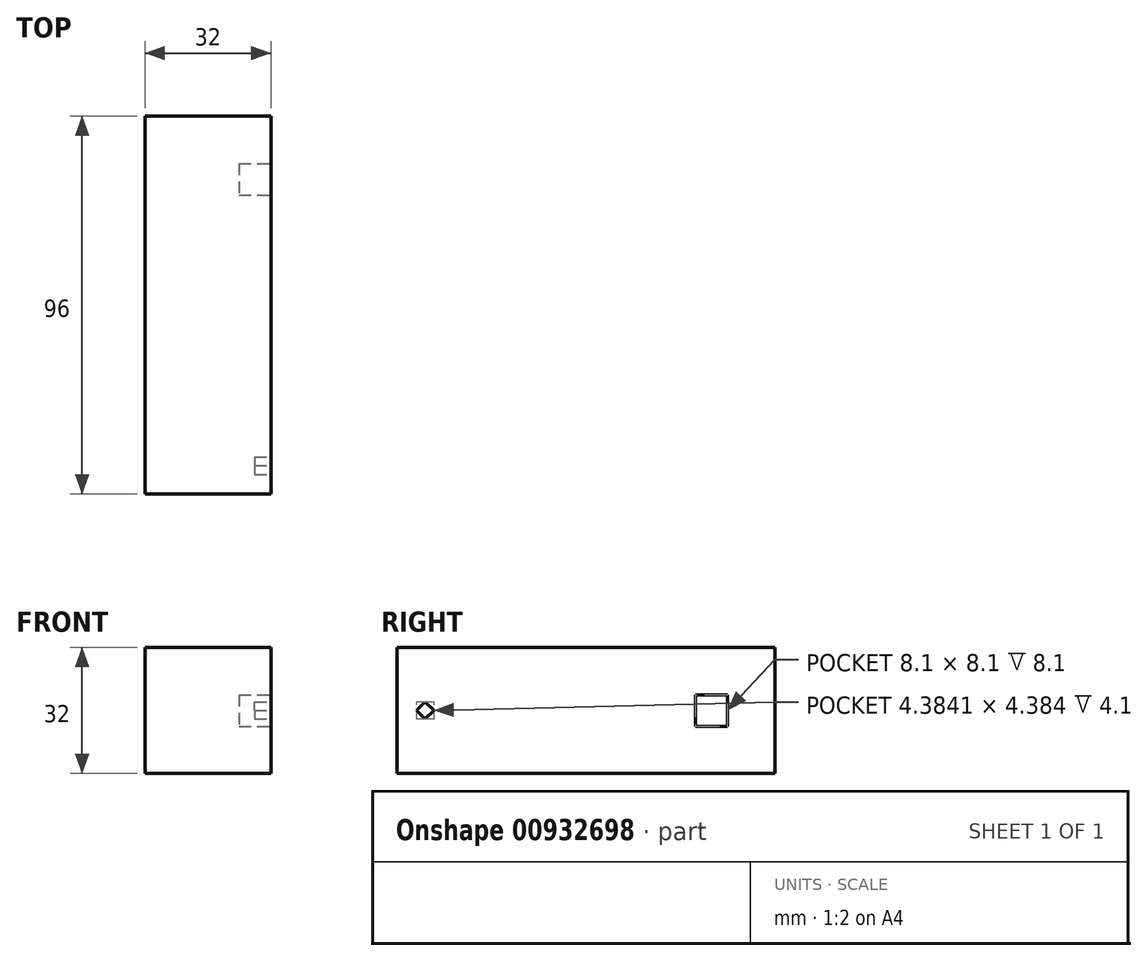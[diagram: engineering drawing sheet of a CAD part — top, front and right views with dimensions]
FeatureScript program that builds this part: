
annotation { "Feature Type Name" : "Feature", "Feature Type Description" : "" }
export const myFeature = defineFeature(function(context is Context, id is Id, definition is map)
    precondition{}
    {
        {
            var Q0;
            Q0=qCreatedBy(makeId("Top.planeOp"),FACE);
            var sketch = newSketch(context, id + "F0", { "sketchPlane" : qUnion([Q0])});
            skLineSegment(sketch, "E0.bottom", {"start": v(-16, 48) * mm, "end": v(16, 48) * mm});
            skLineSegment(sketch, "E0.top", {"start": v(-16, -48) * mm, "end": v(16, -48) * mm});
            skLineSegment(sketch, "E0.left", {"start": v(-16, 48) * mm, "end": v(-16, -48) * mm});
            skLineSegment(sketch, "E0.right", {"start": v(16, 48) * mm, "end": v(16, -48) * mm});
            skSolve(sketch);
        }
        {
            var Q0;
            Q0 = qSketchRegion(id + "F0", true);
            extrude(context, id + "F1", {"entities" : qUnion([Q0]), "depth" : 32 * mm, "offsetDistance" : 25 * mm});
        }
        {
            var Q0;
            Q0=makeQuery(id+"F1.opExtrude","SWEPT_FACE",FACE,{"disambiguationData":[OSD([sQuery(id+"F0.wireOp",EDGE,"E0.right")])]});
            var sketch = newSketch(context, id + "F2", { "sketchPlane" : qUnion([Q0])});
            skLineSegment(sketch, "E1.bottom", {"start": v(36, 20) * mm, "end": v(27.9, 20) * mm});
            skLineSegment(sketch, "E1.top", {"start": v(36, 11.9) * mm, "end": v(27.9, 11.9) * mm});
            skLineSegment(sketch, "E1.left", {"start": v(36, 20) * mm, "end": v(36, 11.9) * mm});
            skLineSegment(sketch, "E1.right", {"start": v(27.9, 20) * mm, "end": v(27.9, 11.9) * mm});
            skSolve(sketch);
        }
        {
            var Q0;
            Q0 = qSketchRegion(id + "F2", true);
            extrude(context, id + "F3", {"entities" : qUnion([Q0]), "operationType" : NewBodyOperationType.REMOVE, "oppositeDirection" : true, "depth" : 8.1 * mm, "offsetDistance" : 25 * mm});
        }
        {
            var Q0;
            Q0=makeQuery(id+"F1.opExtrude","SWEPT_FACE",FACE,{"disambiguationData":[OSD([sQuery(id+"F0.wireOp",EDGE,"E0.right")])]});
            var sketch = newSketch(context, id + "F4", { "sketchPlane" : qUnion([Q0])});
            skLineSegment(sketch, "E2", {"start": v(-40.8, 18.2) * mm, "end": v(-43, 16) * mm});
            skLineSegment(sketch, "E3", {"start": v(-43, 16) * mm, "end": v(-40.8, 13.8) * mm});
            skLineSegment(sketch, "E4", {"start": v(-40.8, 13.8) * mm, "end": v(-38.62, 16) * mm});
            skLineSegment(sketch, "E5", {"start": v(-38.62, 16) * mm, "end": v(-40.8, 18.2) * mm});
            skLineSegment(sketch, "E6", {"start": v(-48, 16) * mm, "end": v(48, 16) * mm, "construction": true});
            skSolve(sketch);
        }
        {
            var Q0;
            Q0 = qSketchRegion(id + "F4", true);
            extrude(context, id + "F5", {"entities" : qUnion([Q0]), "operationType" : NewBodyOperationType.REMOVE, "oppositeDirection" : true, "depth" : 4.1 * mm, "offsetDistance" : 25 * mm});
        }
    });
